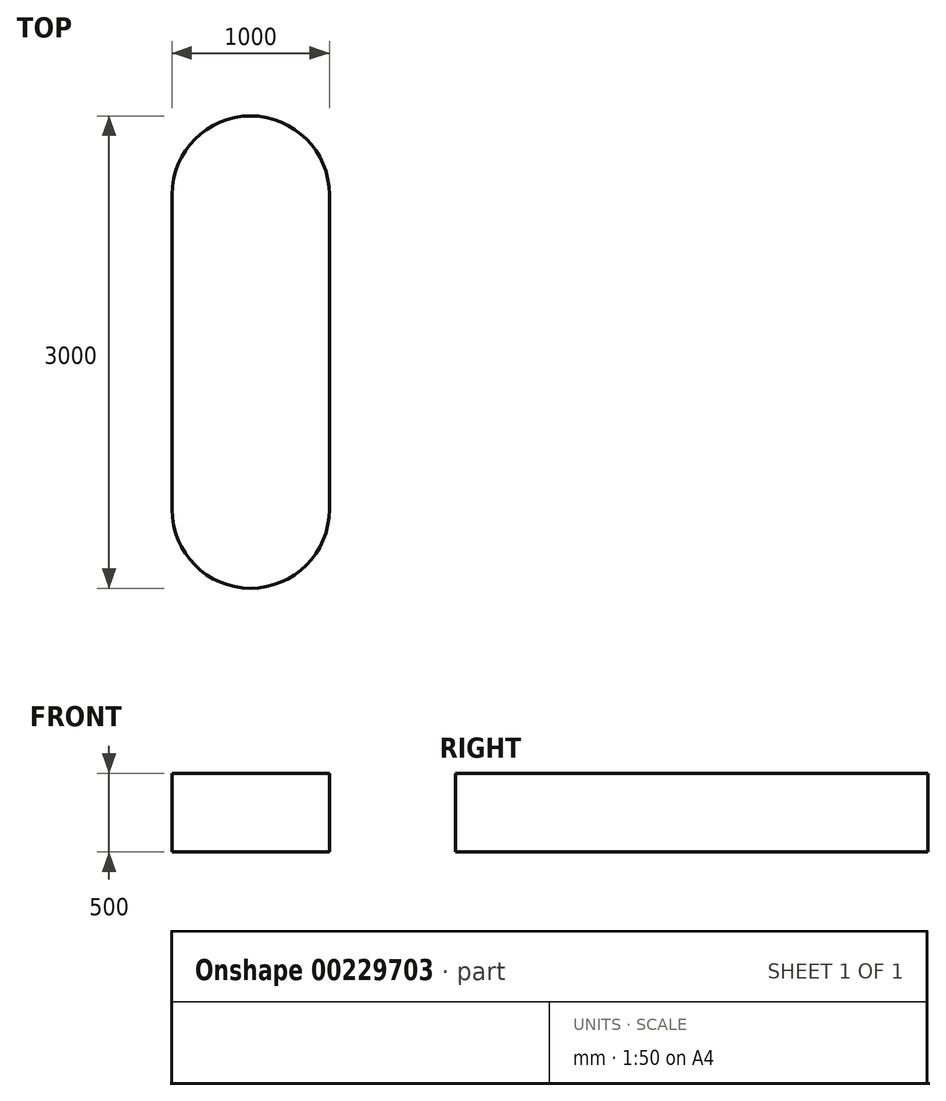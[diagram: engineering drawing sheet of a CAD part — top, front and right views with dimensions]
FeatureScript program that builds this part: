
annotation { "Feature Type Name" : "Feature", "Feature Type Description" : "" }
export const myFeature = defineFeature(function(context is Context, id is Id, definition is map)
    precondition{}
    {
        {
            var Q0;
            Q0=qCreatedBy(makeId("Top.planeOp"),FACE);
            var sketch = newSketch(context, id + "F0", { "sketchPlane" : qUnion([Q0])});
            skLineSegment(sketch, "E0.bottom", {"start": v(-500, 1000) * mm, "end": v(500, 1000) * mm});
            skLineSegment(sketch, "E0.top", {"start": v(-500, -1000) * mm, "end": v(500, -1000) * mm});
            skLineSegment(sketch, "E0.left", {"start": v(-500, 1000) * mm, "end": v(-500, -1000) * mm});
            skLineSegment(sketch, "E0.right", {"start": v(500, 1000) * mm, "end": v(500, -1000) * mm});
            skPoint(sketch, "E0.middle", {"position": v(0, 0) * mm});
            skCircle(sketch, "E1", {"center": v(0, -1000) * mm, "radius": 500 * mm});
            skCircle(sketch, "E2", {"center": v(0, 1000) * mm, "radius": 500 * mm});
            skSolve(sketch);
        }
        {
            var Q0;
            Q0 = qSketchRegion(id + "F0", true);
            extrude(context, id + "F1", {"entities" : qUnion([Q0]), "depth" : 500 * mm});
        }
    });
